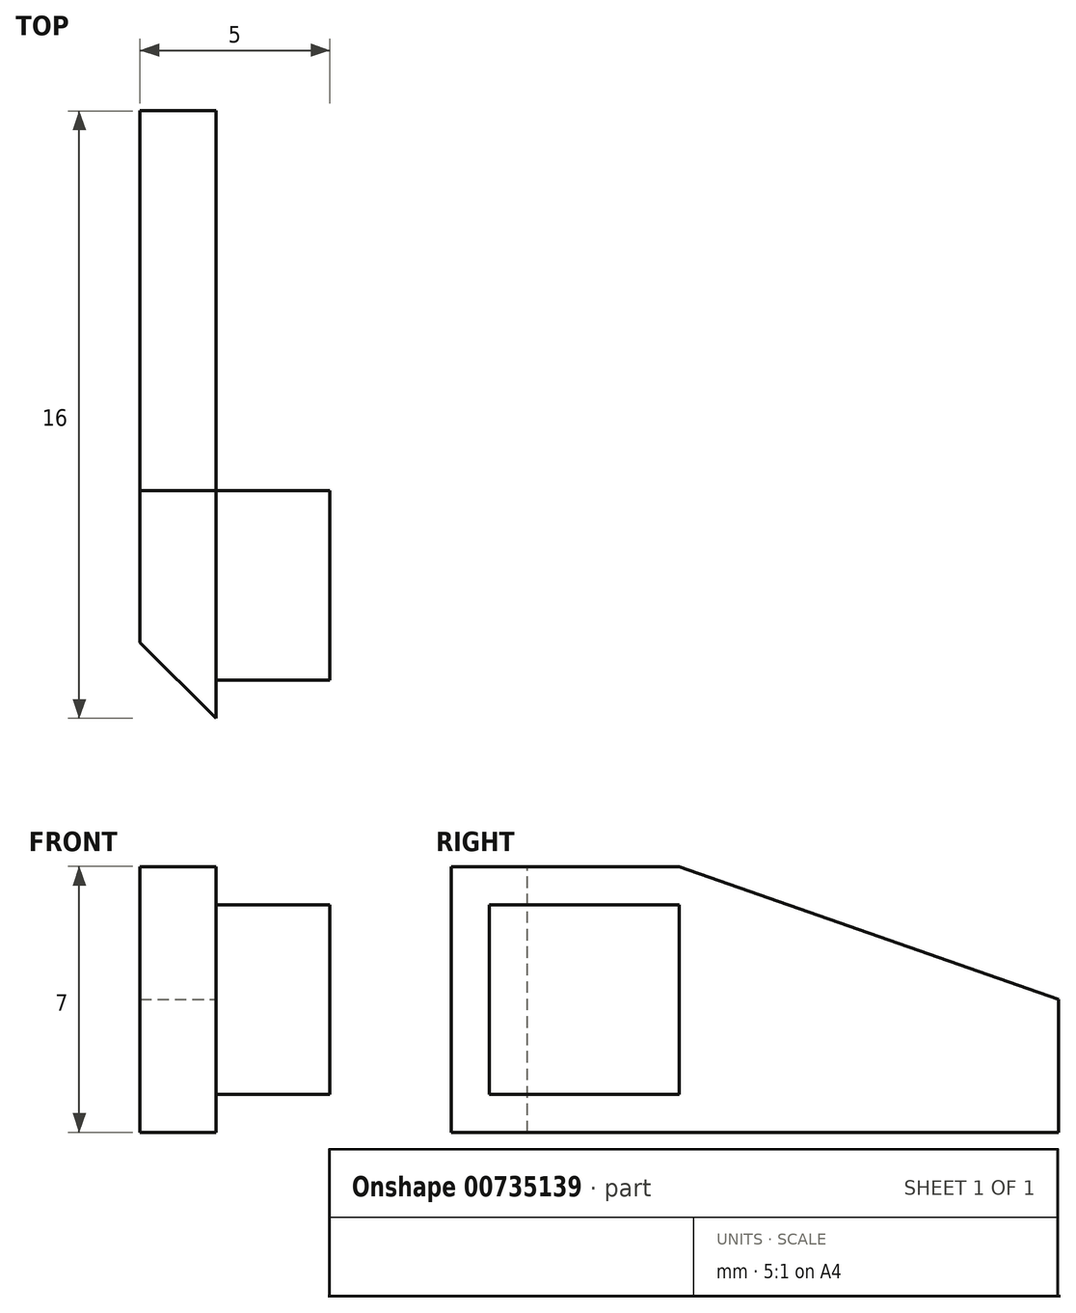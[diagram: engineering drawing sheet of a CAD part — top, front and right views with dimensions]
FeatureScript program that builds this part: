
annotation { "Feature Type Name" : "Feature", "Feature Type Description" : "" }
export const myFeature = defineFeature(function(context is Context, id is Id, definition is map)
    precondition{}
    {
        {
            var Q0;
            Q0=qCreatedBy(makeId("Right.planeOp"),FACE);
            var sketch = newSketch(context, id + "F0", { "sketchPlane" : qUnion([Q0])});
            skLineSegment(sketch, "E0.bottom", {"start": v(43.1, 34.6) * mm, "end": v(38.1, 34.6) * mm});
            skLineSegment(sketch, "E0.top", {"start": v(43.1, 29.6) * mm, "end": v(38.1, 29.6) * mm});
            skLineSegment(sketch, "E0.left", {"start": v(43.1, 34.6) * mm, "end": v(43.1, 29.6) * mm});
            skLineSegment(sketch, "E0.right", {"start": v(38.1, 34.6) * mm, "end": v(38.1, 29.6) * mm});
            skSolve(sketch);
        }
        {
            var Q0;
            Q0=makeQuery(id+"F0.imprint","IMPRINT",FACE,{"disambiguationData":[TD([[makeQuery(id+"F0.imprint","IMPRINT",EDGE,{"derivedFrom":sQuery(id+"F0.wireOp",EDGE,"E0.bottom")}),1.0]])]});
            extrude(context, id + "F1", {"entities" : qUnion([Q0]), "depth" : 3 * mm, "offsetDistance" : 25 * mm});
        }
        {
            var Q0;
            Q0=makeQuery(id+"F1.opExtrude","CAP_FACE",FACE,{"disambiguationData":[OSD([sQuery(id+"F0.wireOp",EDGE,"E0.bottom"),sQuery(id+"F0.wireOp",EDGE,"E0.top"),sQuery(id+"F0.wireOp",EDGE,"E0.left"),sQuery(id+"F0.wireOp",EDGE,"E0.right")])],"isStart":true});
            var sketch = newSketch(context, id + "F2", { "sketchPlane" : qUnion([Q0])});
            skLineSegment(sketch, "E1.bottom", {"start": v(-37.1, 35.6) * mm, "end": v(-53.1, 35.6) * mm});
            skLineSegment(sketch, "E1.top", {"start": v(-37.1, 28.6) * mm, "end": v(-53.1, 28.6) * mm});
            skLineSegment(sketch, "E1.left", {"start": v(-37.1, 35.6) * mm, "end": v(-37.1, 28.6) * mm});
            skLineSegment(sketch, "E1.right", {"start": v(-53.1, 35.6) * mm, "end": v(-53.1, 28.6) * mm});
            skLineSegment(sketch, "E2", {"start": v(-53.1, 32.1) * mm, "end": v(-43.1, 35.6) * mm});
            skLineSegment(sketch, "E3", {"start": v(-43.1, 35.6) * mm, "end": v(-43.1, 28.6) * mm});
            skLineSegment(sketch, "E4", {"start": v(-43.1, 28.6) * mm, "end": v(-53.1, 32.1) * mm});
            skLineSegment(sketch, "E5", {"start": v(-51.1, 35.6) * mm, "end": v(-51.1, 28.6) * mm});
            skSolve(sketch);
        }
        {
            var Q0;
            Q0=makeQuery(id+"F2.imprint","IMPRINT",FACE,{"disambiguationData":[TD([[makeQuery(id+"F2.imprint","IMPRINT",EDGE,{"derivedFrom":makeQuery(id+"F1.opExtrude","CAP_EDGE",EDGE,{"disambiguationData":[OSD([sQuery(id+"F0.wireOp",EDGE,"E0.bottom")])],"isStart":true})}),-1.0]])]});
            var Q1;
            {var subQ4=sQuery(id+"F2.wireOp",EDGE,"E1.left");Q1=makeQuery(id+"F2.imprint","IMPRINT",FACE,{"disambiguationData":[TD([[makeQuery(id+"F2.imprint","IMPRINT",EDGE,{"derivedFrom":subQ4}),-1.0]])]});}
            var Q2;
            {var subQ0=sQuery(id+"F2.wireOp",EDGE,"E3");var subQ4=makeQuery(id+"F2.imprint","INTERSECT",VERTEX,{"derivedFrom":[makeQuery(id+"F1.opExtrude","CAP_EDGE",EDGE,{"disambiguationData":[OSD([sQuery(id+"F0.wireOp",EDGE,"E0.bottom")])],"isStart":true}),subQ0]});Q2=makeQuery(id+"F2.imprint","IMPRINT",FACE,{"disambiguationData":[TD([[makeQuery(id+"F2.imprint","IMPRINT",EDGE,{"disambiguationData":[TD([[subQ4,-1.0]])],"derivedFrom":subQ0}),-1.0]])]});}
            var Q3;
            {var subQ1=sQuery(id+"F2.wireOp",EDGE,"E2");var subQ3=sQuery(id+"F2.wireOp",EDGE,"E5");var subQ4=makeQuery(id+"F2.imprint","INTERSECT",VERTEX,{"derivedFrom":[subQ1,subQ3]});Q3=makeQuery(id+"F2.imprint","IMPRINT",FACE,{"disambiguationData":[TD([[makeQuery(id+"F2.imprint","IMPRINT",EDGE,{"disambiguationData":[TD([[subQ4,-1.0]])],"derivedFrom":subQ3}),-1.0]])]});}
            var Q4;
            {var subQ0=sQuery(id+"F2.wireOp",EDGE,"E1.right");var subQ1=sQuery(id+"F2.wireOp",EDGE,"E1.top");var subQ2=makeQuery(id+"F2.imprint","INTERSECT",VERTEX,{"derivedFrom":[subQ1,subQ0]});Q4=makeQuery(id+"F2.imprint","IMPRINT",FACE,{"disambiguationData":[TD([[makeQuery(id+"F2.imprint","IMPRINT",EDGE,{"disambiguationData":[TD([[subQ2,1.0]])],"derivedFrom":subQ1}),-1.0]])]});}
            var Q5;
            {var subQ1=sQuery(id+"F2.wireOp",EDGE,"E1.top");var subQ3=sQuery(id+"F2.wireOp",EDGE,"E5");var subQ4=makeQuery(id+"F2.imprint","INTERSECT",VERTEX,{"derivedFrom":[subQ1,subQ3]});Q5=makeQuery(id+"F2.imprint","IMPRINT",FACE,{"disambiguationData":[TD([[makeQuery(id+"F2.imprint","IMPRINT",EDGE,{"disambiguationData":[TD([[subQ4,1.0]])],"derivedFrom":subQ3}),1.0]])]});}
            extrude(context, id + "F3", {"entities" : qUnion([Q0, Q1, Q2, Q3, Q4, Q5]), "operationType" : NewBodyOperationType.ADD, "depth" : 2 * mm, "offsetDistance" : 25 * mm});
        }
        {
            var Q0;
            Q0=makeQuery(id+"F3.opExtrude","CAP_EDGE",EDGE,{"disambiguationData":[OSD([sQuery(id+"F2.wireOp",EDGE,"E1.left")])],"isStart":false});
            chamfer(context, id + "F4", {"entities" : qUnion([Q0]), "width" : 2 * mm, "tangentPropagation" : true});
        }
    });
